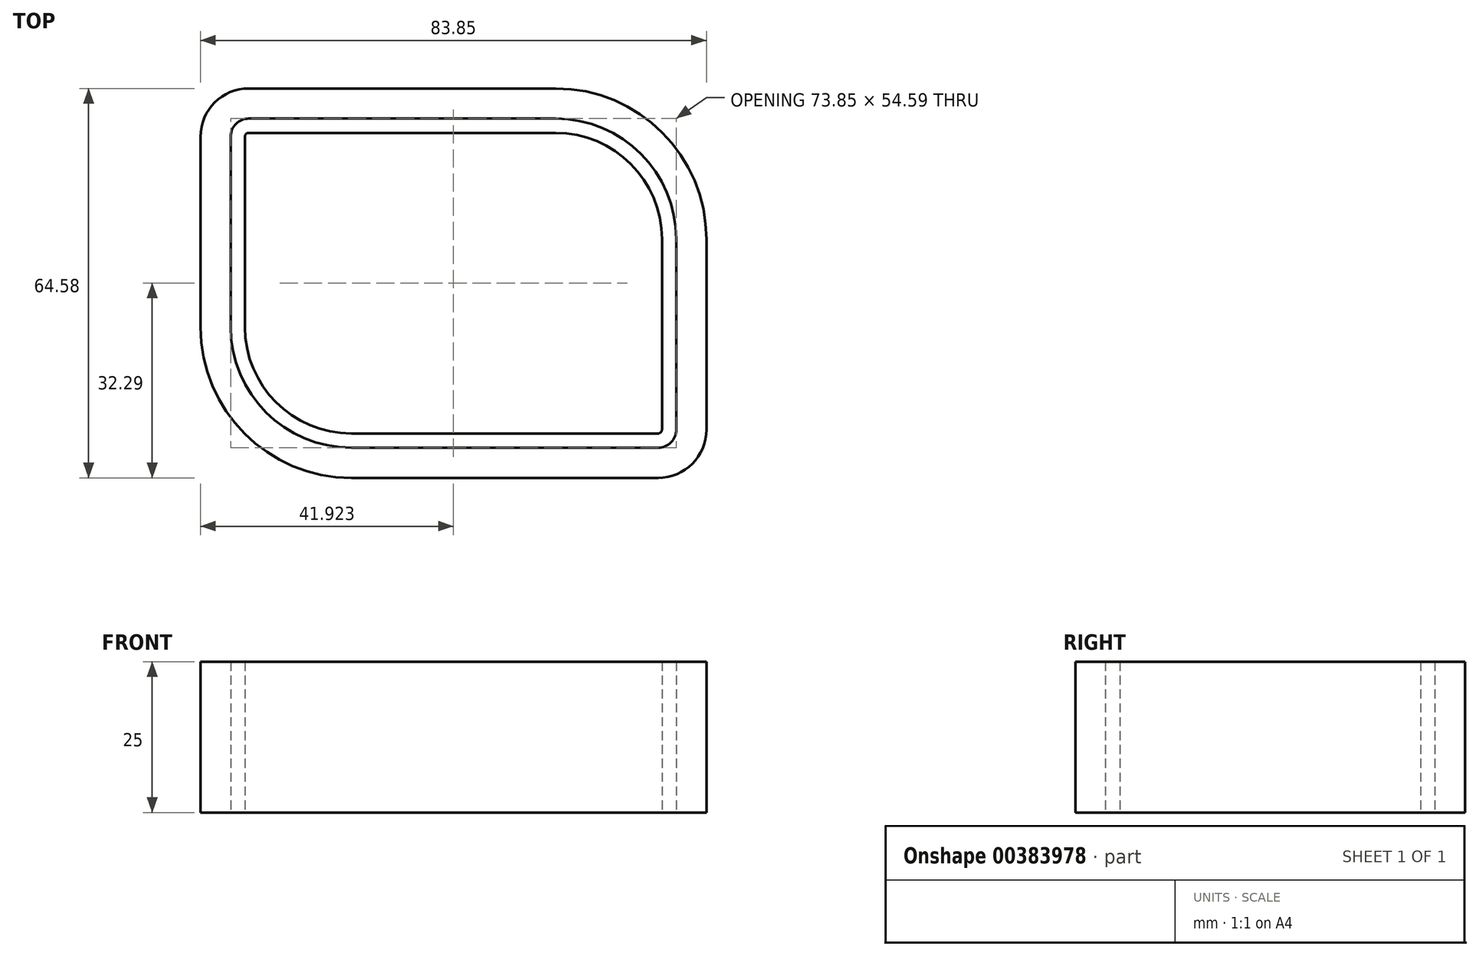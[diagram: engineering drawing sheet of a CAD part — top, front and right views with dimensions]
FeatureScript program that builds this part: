
annotation { "Feature Type Name" : "Feature", "Feature Type Description" : "" }
export const myFeature = defineFeature(function(context is Context, id is Id, definition is map)
    precondition{}
    {
        {
            var Q0;
            Q0=qCreatedBy(makeId("Top.planeOp"),FACE);
            var sketch = newSketch(context, id + "F0", { "sketchPlane" : qUnion([Q0])});
            skLineSegment(sketch, "E0.bottom", {"start": v(-31.94, 32.3) * mm, "end": v(18.9, 32.3) * mm});
            skLineSegment(sketch, "E0.top", {"start": v(-14.94, -32.3) * mm, "end": v(35.9, -32.3) * mm});
            skLineSegment(sketch, "E0.left", {"start": v(-39.94, 24.3) * mm, "end": v(-39.94, -7.3) * mm});
            skLineSegment(sketch, "E0.right", {"start": v(43.9, 7.3) * mm, "end": v(43.9, -24.3) * mm});
            skPoint(sketch, "E0.middle", {"position": v(1.98, 0) * mm});
            skPoint(sketch, "E1.visualSharp", {"position": v(-39.94, 32.3) * mm});
            skArc(sketch, "E1.filletArc", {"start": v(-31.94, 32.3) * mm, "mid": v(-37.6, 29.95) * mm, "end": v(-39.94, 24.3) * mm});
            skPoint(sketch, "E2.visualSharp", {"position": v(43.9, -32.3) * mm});
            skArc(sketch, "E2.filletArc", {"start": v(35.9, -32.3) * mm, "mid": v(41.56, -29.95) * mm, "end": v(43.9, -24.3) * mm});
            skPoint(sketch, "E3.visualSharp", {"position": v(43.9, 32.3) * mm});
            skArc(sketch, "E3.filletArc", {"start": v(43.9, 7.3) * mm, "mid": v(36.59, 24.97) * mm, "end": v(18.9, 32.3) * mm});
            skPoint(sketch, "E4.visualSharp", {"position": v(-39.94, -32.3) * mm});
            skArc(sketch, "E4.filletArc", {"start": v(-39.94, -7.3) * mm, "mid": v(-32.62, -24.97) * mm, "end": v(-14.94, -32.3) * mm});
            skArc(sketch, "E5.0", {"start": v(-31.94, 24.93) * mm, "mid": v(-32.4, 24.74) * mm, "end": v(-32.58, 24.3) * mm});
            skLineSegment(sketch, "E5.1", {"start": v(-32.58, 24.3) * mm, "end": v(-32.58, -7.3) * mm});
            skLineSegment(sketch, "E5.2", {"start": v(-31.94, 24.93) * mm, "end": v(18.9, 24.93) * mm});
            skArc(sketch, "E5.3", {"start": v(-32.58, -7.3) * mm, "mid": v(-27.41, -19.76) * mm, "end": v(-14.94, -24.93) * mm});
            skArc(sketch, "E5.4", {"start": v(36.54, 7.3) * mm, "mid": v(31.38, 19.76) * mm, "end": v(18.9, 24.93) * mm});
            skLineSegment(sketch, "E5.5", {"start": v(36.54, 7.3) * mm, "end": v(36.54, -24.3) * mm});
            skArc(sketch, "E5.6", {"start": v(35.9, -24.93) * mm, "mid": v(36.36, -24.74) * mm, "end": v(36.54, -24.3) * mm});
            skLineSegment(sketch, "E5.7", {"start": v(-14.94, -24.93) * mm, "end": v(35.9, -24.93) * mm});
            skArc(sketch, "E6.0", {"start": v(-31.94, 27.3) * mm, "mid": v(-34.06, 26.41) * mm, "end": v(-34.94, 24.3) * mm});
            skLineSegment(sketch, "E6.1", {"start": v(-34.94, 24.3) * mm, "end": v(-34.94, -7.3) * mm});
            skLineSegment(sketch, "E6.2", {"start": v(-31.94, 27.3) * mm, "end": v(18.9, 27.3) * mm});
            skArc(sketch, "E6.3", {"start": v(-34.94, -7.3) * mm, "mid": v(-29.08, -21.44) * mm, "end": v(-14.94, -27.3) * mm});
            skArc(sketch, "E6.4", {"start": v(38.9, 7.3) * mm, "mid": v(33.05, 21.44) * mm, "end": v(18.9, 27.3) * mm});
            skLineSegment(sketch, "E6.5", {"start": v(38.9, 7.3) * mm, "end": v(38.9, -24.3) * mm});
            skArc(sketch, "E6.6", {"start": v(35.9, -27.3) * mm, "mid": v(38.03, -26.41) * mm, "end": v(38.9, -24.3) * mm});
            skLineSegment(sketch, "E6.7", {"start": v(-14.94, -27.3) * mm, "end": v(35.9, -27.3) * mm});
            skSolve(sketch);
        }
        {
            var Q0;
            Q0 = qSketchRegion(id + "F0", true);
            var Q1;
            Q1=makeQuery(id+"F0.imprint","IMPRINT",FACE,{"disambiguationData":[TD([[makeQuery(id+"F0.imprint","IMPRINT",EDGE,{"derivedFrom":sQuery(id+"F0.wireOp",EDGE,"E5.0")}),1.0]])]});
            extrude(context, id + "F1", {"entities" : qUnion([Q0, Q1]), "depth" : 25 * mm});
        }
    });
